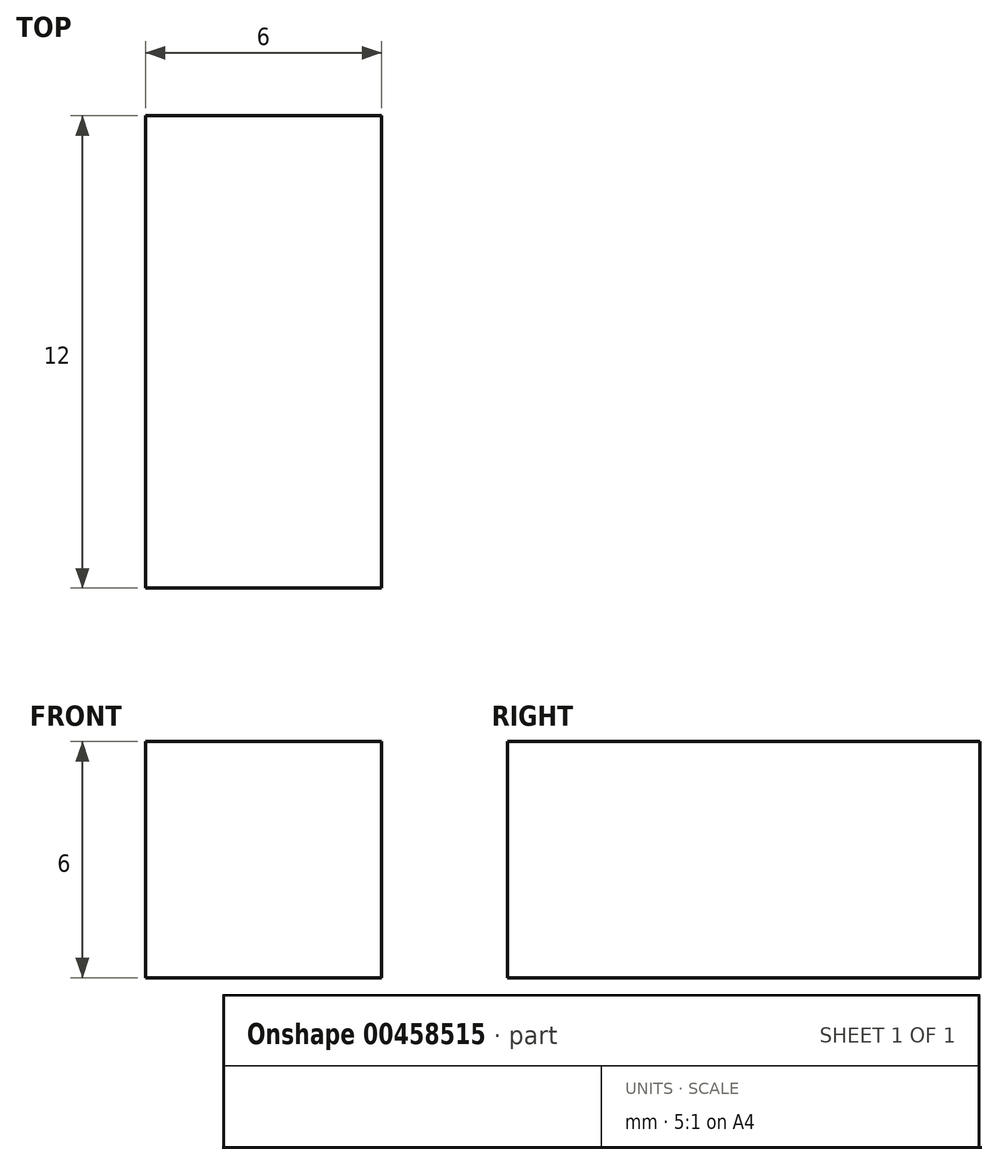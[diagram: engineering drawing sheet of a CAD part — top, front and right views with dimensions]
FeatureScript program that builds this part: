
annotation { "Feature Type Name" : "Feature", "Feature Type Description" : "" }
export const myFeature = defineFeature(function(context is Context, id is Id, definition is map)
    precondition{}
    {
        {
            var Q0;
            Q0=qCreatedBy(makeId("Front.planeOp"),FACE);
            var sketch = newSketch(context, id + "F0", { "sketchPlane" : qUnion([Q0])});
            skLineSegment(sketch, "E0.bottom", {"start": v(3, -3) * mm, "end": v(-3, -3) * mm});
            skLineSegment(sketch, "E0.top", {"start": v(3, 3) * mm, "end": v(-3, 3) * mm});
            skLineSegment(sketch, "E0.left", {"start": v(3, -3) * mm, "end": v(3, 3) * mm});
            skLineSegment(sketch, "E0.right", {"start": v(-3, -3) * mm, "end": v(-3, 3) * mm});
            skPoint(sketch, "E0.middle", {"position": v(0, 0) * mm});
            skSolve(sketch);
        }
        {
            var Q0;
            Q0=makeQuery(id+"F0.imprint","IMPRINT",FACE,{"disambiguationData":[TD([[makeQuery(id+"F0.imprint","IMPRINT",EDGE,{"derivedFrom":sQuery(id+"F0.wireOp",EDGE,"E0.bottom")}),-1.0]])]});
            extrude(context, id + "F1", {"entities" : qUnion([Q0]), "depth" : 12 * mm});
        }
    });
